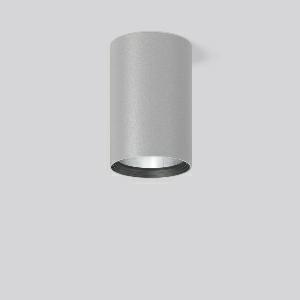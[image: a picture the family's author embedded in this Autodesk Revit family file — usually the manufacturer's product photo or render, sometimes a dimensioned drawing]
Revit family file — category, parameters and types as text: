
# Revit family: heledon_maxi_a_931219_004_76_1cb0
name_source: partatom
category: Lighting Fixtures
units: mm (PartAtom-declared; Revit-internal decimal feet)

## family parameters
Cut with Voids When Loaded = No
Host = Face
Light Source = No
Part Type = Normal
Room Calculation Point = No
Round Connector Dimension = Use Diameter
Shared = No

## types (1)
- HELEDON maxi A (1 x LED Modul 930, 3250 lm, 3000)
    Apparent Load = 25 VA
    Approval mark = CE
    CIE Flux Codes = 97 100 100 100 100
    Color Rendering = 90
    Color Temperature = 3000
    Default Elevation = 1800 mm
    Description = Series: HELEDON maxi
Cylindrical surface-mounted downlight. Housing: die-cast aluminium, powder-coated. Internal ceiling frame polycarbonate with bayonet mounting. Black plastic ring and recessed LED to prevent glare from the side. Optical assembly with reflector made of MIRO-Silver with 98% total light reflection for outstanding efficiency - can be changed without tools. Best colour rendering index Ra>90. Suitable for Ceiling mounting. Easy installation with a separate ceiling frame with bayonet mounting and plug connection. Driver integrated. Connected via plug-in connector. High quality converter without flickering and stroboscopic effect. The following accessories can be mounted without use of tools: interchangeable lenses, decorative glasses, honeycomb louvre, clear and frosted diffusers, white interchangeable plastic ring. 
Colour: silver
Diameter: 123 mm
Height: 183 mm
Lamp: LED
Socket: without socket
Colour temperature: 3000K
Colour rendering index (CRI): 92
System power: 25 W
Rated luminous flux: 3250 lm
Luminous efficiency: 130 lm/W
Control gear: Converter, dimmable, DALI
Protection class: I
Type of protection: IP 20
    Height = 183 mm
    Lamp = 1 x LED Modul 930
    Lamp Light Flux = 3250 lm
    Lamp count = 1
    Length = 123 mm
    Lifetime = 50000 h
    Luminous efficacy = 130 lm/W
    Manufacturer = RZB
    ModVariant = No
    Model = 931219.004.76
    Mounting Place = Ceiling
    Mounting Type = Surface mounted
    Number of Poles = 1
    OnlyDefault = Yes
    Power Factor = 1
    Product Name = HELEDON maxi A
    Product group = Surface mounted downlights
    ProductGroupID = 302
    Protection Class = Protection class I
    Protection Degree = IP 20
    RLX_Detail_Level = 1
    RLX_Emergency_Light_Flux = 0 lm
    RLX_Emergency_Type = 0
    RLX_Emergency_Type_DB = No
    RlxData = <blob elided: 98501 chars, md5=2f0cb0e1>
    Socket = socket
    Standby Power = 0 W
    System Light Flux = 3250 lm
    System Power = 25 W
    Type Comments = Product without accessories
    Type Image = 931192.004.jpg
    URL = http://relux.com
    VarID = ---
    Voltage = 230 V
    Voltage Range = 220-240 V
    Weight = 0.00 kg
    Width = 0 mm  [stored 0 ft]

note: [stored X ft] marks values corroborated as IEEE doubles in the binary element streams (Revit-internal decimal feet)

## geometry (parser evidence)
native form markers: Blend x4, Sweep x10
no freeform markers — native parametric forms only
